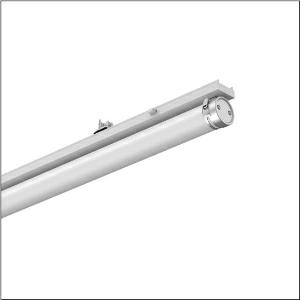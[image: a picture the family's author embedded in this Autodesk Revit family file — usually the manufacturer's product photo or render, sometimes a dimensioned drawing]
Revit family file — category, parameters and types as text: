
# Revit family: monsun_r__31_tube_51ft10mn4a0atr2_ffb0
name_source: partatom
category: Lighting Fixtures
units: mm (PartAtom-declared; Revit-internal decimal feet)

## family parameters
Cut with Voids When Loaded = No
Host = Face
Light Source = No
Part Type = Normal
Room Calculation Point = No
Round Connector Dimension = Use Diameter
Shared = No

## types (1)
- --- (1 x LED, 10000 lm, 58 W, 4000K)
    Apparent Load = 58 VA
    CIE Flux Codes = 42 71 90 91 100
    Color Rendering = 80
    Color Temperature = 4000K
    Default Elevation = 1800 mm
    Description = Monsun® 31 Tube, tubular luminaire, primary optical cover: diffuser, of PMMA, light emission: direct distribution, primary light characteristic: symmetric, LED, rated luminous flux: 10.000lm, luminous efficacy: 172lm/W, light colour: 840, colour temperature: 4000K, with with 1 terminal, 3-pole, max. 2.5mm², mains connection: 220..240V, AC, 50/60Hz, rated input power: 58W, housing, cylindrical, of PMMA, semi-transparent, matt white, with luminaire and ceiling fastening, V4A, mounting with brackets of stainless steel, length: 1.500mm, diameter: 75mm, end cap, of stainless steel (V4A), protection rating (complete): IP20, protection rating (lamp compartment): IP67/69K, insulation class (complete): insulation class I (protective earthing), certification: CE, UKCA, impact resistance: IK06, permissible operating ambient temperature: -20..+40°C, corresponds to IFS (International Featured Standards) requirements for safety and quality in the food industry, contact your sales advisor before using the luminaires in applications with unclear chemical exposure, large temperature fluctuations or condensation-forming humidity, packaging unit: 1 piece
    Height = 132 mm
    Lamp = 1 x LED
    Lamp Light Flux = 10000 lm
    Lamp Power = 58 W
    Lamp count = 1
    Length = 1500 mm
    Luminous efficacy = 172 lm/W
    Manufacturer = Siteco
    ModVariant = No
    Model = 51FT10MN4A0ATR2
    Mounting Place = Ceiling
    Mounting Type = Pendant
    Number of Poles = 1
    OnlyDefault = Yes
    Power Factor = 1
    Product Name = Monsun® 31 Tube
    Product group = tubular luminaire
    ProductGroupID = 906
    Protection Class = Protection class I
    Protection Degree = IP 20
    RLX_Detail_Level = 1
    RLX_Emergency_Light_Flux = 0 lm
    RLX_Emergency_Type = 0
    RLX_Emergency_Type_DB = No
    RlxData = <blob elided: 32289 chars, md5=94ff9062>
    Socket = socket
    Standby Power = 0 W
    System Light Flux = 10000 lm
    System Power = 58 W
    Type Comments = factory setting: luminous flux: 100 % | (OFF | OFF | OFF | OFF) | 350 mA
    Type Image = l_1242814.jpg
    URL = http://relux.com
    VarID = @adj_074687
    Voltage = 0 V
    Weight = 0.00 kg
    Width = 79 mm

## geometry (parser evidence)
native form markers: Blend x4, Sweep x12
no freeform markers — native parametric forms only
